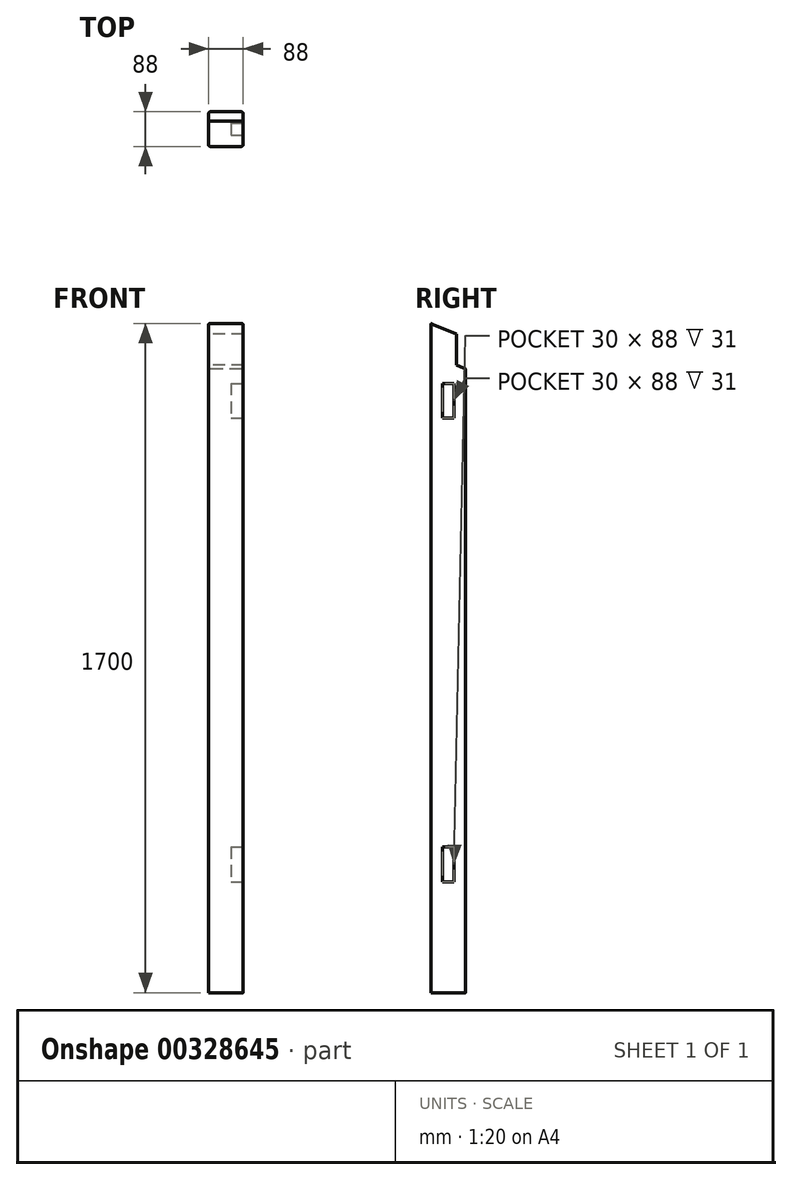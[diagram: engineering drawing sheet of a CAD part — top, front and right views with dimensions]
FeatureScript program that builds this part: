
annotation { "Feature Type Name" : "Feature", "Feature Type Description" : "" }
export const myFeature = defineFeature(function(context is Context, id is Id, definition is map)
    precondition{}
    {
        {
            var Q0;
            Q0=qCreatedBy(makeId("Top.planeOp"),FACE);
            var sketch = newSketch(context, id + "F0", { "sketchPlane" : qUnion([Q0])});
            skLineSegment(sketch, "E0.bottom", {"start": v(0, 0) * mm, "end": v(88, 0) * mm});
            skLineSegment(sketch, "E0.top", {"start": v(0, 88) * mm, "end": v(88, 88) * mm});
            skLineSegment(sketch, "E0.left", {"start": v(0, 0) * mm, "end": v(0, 88) * mm});
            skLineSegment(sketch, "E0.right", {"start": v(88, 0) * mm, "end": v(88, 88) * mm});
            skSolve(sketch);
        }
        {
            var Q0;
            Q0=qSketchRegion(id+"F0",true);
            extrude(context, id + "F1", {"entities" : qUnion([Q0]), "depth" : 1700 * mm});
        }
        {
            var Q0;
            Q0=makeQuery(id+"F1.opExtrude","SWEPT_FACE",FACE,{"disambiguationData":[OSD([sQuery(id+"F0.wireOp",EDGE,"E0.left")])]});
            var sketch = newSketch(context, id + "F2", { "sketchPlane" : qUnion([Q0])});
            skLineSegment(sketch, "E1", {"start": v(0, 1700) * mm, "end": v(-88, 1663.55) * mm});
            skLineSegment(sketch, "E2", {"start": v(-88, 1663.55) * mm, "end": v(-88, 1700) * mm});
            skLineSegment(sketch, "E3", {"start": v(-88, 1700) * mm, "end": v(0, 1700) * mm});
            skSolve(sketch);
        }
        {
            var Q0;
            Q0=qSketchRegion(id+"F2",true);
            extrude(context, id + "F3", {"entities" : qUnion([Q0]), "operationType" : NewBodyOperationType.REMOVE, "endBound" : BoundingType.THROUGH_ALL, "oppositeDirection" : true, "depth" : 351.8 * mm});
        }
        {
            var Q0;
            Q0=makeQuery(id+"F1.opExtrude","SWEPT_FACE",FACE,{"disambiguationData":[OSD([sQuery(id+"F0.wireOp",EDGE,"E0.left")])]});
            var sketch = newSketch(context, id + "F4", { "sketchPlane" : qUnion([Q0])});
            skLineSegment(sketch, "E4", {"start": v(-65, 1673.08) * mm, "end": v(-65, 1594.08) * mm});
            skLineSegment(sketch, "E5", {"start": v(-88, 1663.55) * mm, "end": v(-65, 1673.08) * mm});
            skLineSegment(sketch, "E6", {"start": v(-65, 1594.08) * mm, "end": v(-88, 1584.55) * mm});
            skLineSegment(sketch, "E7", {"start": v(-88, 1663.55) * mm, "end": v(-88, 1584.55) * mm});
            skSolve(sketch);
        }
        {
            var Q0;
            Q0=qSketchRegion(id+"F4",true);
            extrude(context, id + "F5", {"entities" : qUnion([Q0]), "operationType" : NewBodyOperationType.REMOVE, "endBound" : BoundingType.THROUGH_ALL, "oppositeDirection" : true, "depth" : 529.35 * mm});
        }
        {
            var Q0;
            Q0=makeQuery(id+"F1.opExtrude","SWEPT_FACE",FACE,{"disambiguationData":[OSD([sQuery(id+"F0.wireOp",EDGE,"E0.right")])]});
            var sketch = newSketch(context, id + "F6", { "sketchPlane" : qUnion([Q0])});
            skLineSegment(sketch, "E8", {"start": v(44, 0) * mm, "end": v(44, 282) * mm, "construction": true});
            skPoint(sketch, "E8.endSnap0", {"position": v(44, 0) * mm});
            skLineSegment(sketch, "E9", {"start": v(44, 282) * mm, "end": v(29, 282) * mm});
            skLineSegment(sketch, "E10", {"start": v(29, 282) * mm, "end": v(29, 370) * mm});
            skLineSegment(sketch, "E11", {"start": v(29, 370) * mm, "end": v(59, 370) * mm});
            skLineSegment(sketch, "E12", {"start": v(59, 370) * mm, "end": v(59, 282) * mm});
            skLineSegment(sketch, "E13", {"start": v(59, 282) * mm, "end": v(44, 282) * mm});
            skSolve(sketch);
        }
        {
            var Q0;
            Q0=qSketchRegion(id+"F6",true);
            extrude(context, id + "F7", {"entities" : qUnion([Q0]), "operationType" : NewBodyOperationType.REMOVE, "oppositeDirection" : true, "depth" : 31 * mm});
        }
        {
            var Q0;
            Q0=makeQuery(id+"F1.opExtrude","SWEPT_FACE",FACE,{"disambiguationData":[OSD([sQuery(id+"F0.wireOp",EDGE,"E0.right")])]});
            var sketch = newSketch(context, id + "F8", { "sketchPlane" : qUnion([Q0])});
            skLineSegment(sketch, "E14", {"start": v(44, 0) * mm, "end": v(44, 1460) * mm, "construction": true});
            skPoint(sketch, "E14.endSnap0", {"position": v(44, 370) * mm});
            skLineSegment(sketch, "E15", {"start": v(44, 1460) * mm, "end": v(29, 1460) * mm});
            skLineSegment(sketch, "E16", {"start": v(29, 1460) * mm, "end": v(29, 1548) * mm});
            skLineSegment(sketch, "E17", {"start": v(29, 1548) * mm, "end": v(59, 1548) * mm});
            skLineSegment(sketch, "E18", {"start": v(59, 1548) * mm, "end": v(59, 1460) * mm});
            skLineSegment(sketch, "E19", {"start": v(59, 1460) * mm, "end": v(44, 1460) * mm});
            skSolve(sketch);
        }
        {
            var Q0;
            Q0=qSketchRegion(id+"F8",true);
            extrude(context, id + "F9", {"entities" : qUnion([Q0]), "operationType" : NewBodyOperationType.REMOVE, "oppositeDirection" : true, "depth" : 31 * mm});
        }
        {
            var Q0;
            Q0=makeQuery(id+"F1.opExtrude","SWEPT_EDGE",EDGE,{"disambiguationData":[OSD([sQuery(id+"F0.wireOp",EDGE,"E0.bottom"),sQuery(id+"F0.wireOp",EDGE,"E0.right")])]});
            var Q1;
            Q1=makeQuery(id+"F1.opExtrude","SWEPT_EDGE",EDGE,{"disambiguationData":[OSD([sQuery(id+"F0.wireOp",EDGE,"E0.bottom"),sQuery(id+"F0.wireOp",EDGE,"E0.left")])]});
            var Q2;
            Q2=makeQuery(id+"F1.opExtrude","SWEPT_EDGE",EDGE,{"disambiguationData":[OSD([sQuery(id+"F0.wireOp",EDGE,"E0.top"),sQuery(id+"F0.wireOp",EDGE,"E0.right")])]});
            var Q3;
            Q3=makeQuery(id+"F1.opExtrude","SWEPT_EDGE",EDGE,{"disambiguationData":[OSD([sQuery(id+"F0.wireOp",EDGE,"E0.top"),sQuery(id+"F0.wireOp",EDGE,"E0.left")])]});
            fillet(context, id + "F10", {"entities" : qUnion([Q0, Q1, Q2, Q3]), "radius" : 5 * mm, "tangentPropagation" : true, "allowEdgeOverflow" : false});
        }
    });
